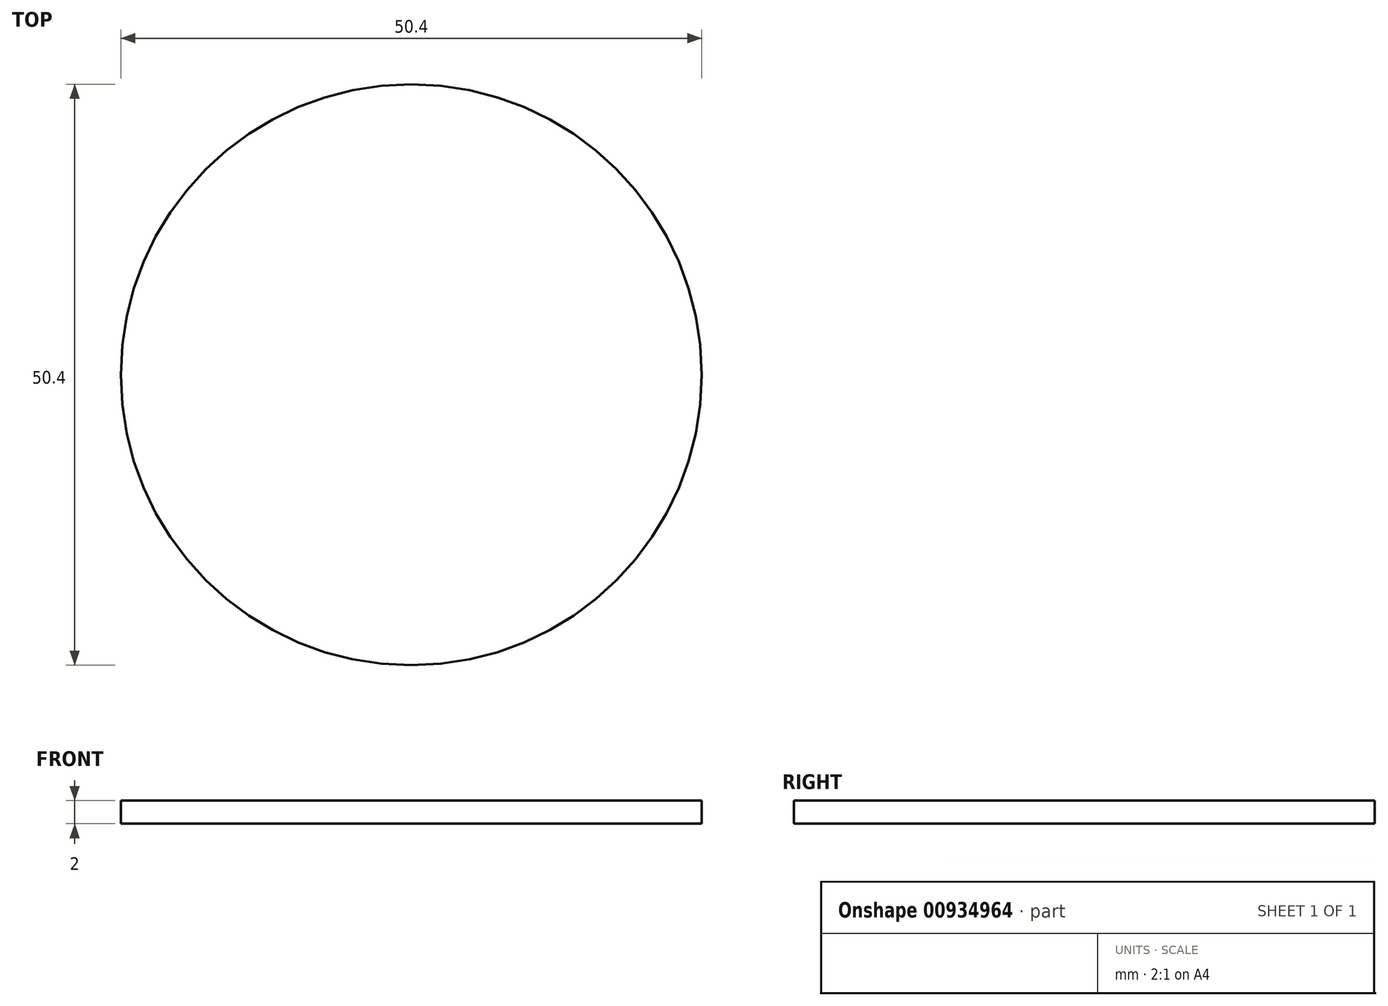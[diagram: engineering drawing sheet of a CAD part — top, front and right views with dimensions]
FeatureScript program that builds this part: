
annotation { "Feature Type Name" : "Feature", "Feature Type Description" : "" }
export const myFeature = defineFeature(function(context is Context, id is Id, definition is map)
    precondition{}
    {
        {
            var Q0;
            Q0=qCreatedBy(makeId("Top.planeOp"),FACE);
            var sketch = newSketch(context, id + "F0", { "sketchPlane" : qUnion([Q0])});
            skCircle(sketch, "E0", {"center": v(0, 0) * mm, "radius": 25.2 * mm});
            skSolve(sketch);
        }
        {
            var Q0;
            Q0=makeQuery(id+"F0.imprint","IMPRINT",FACE,{"disambiguationData":[TD([[makeQuery(id+"F0.imprint","IMPRINT",EDGE,{"derivedFrom":sQuery(id+"F0.wireOp",EDGE,"E0")}),1.0]])]});
            extrude(context, id + "F1", {"entities" : qUnion([Q0]), "depth" : 2 * mm, "offsetDistance" : 25 * mm});
        }
    });
